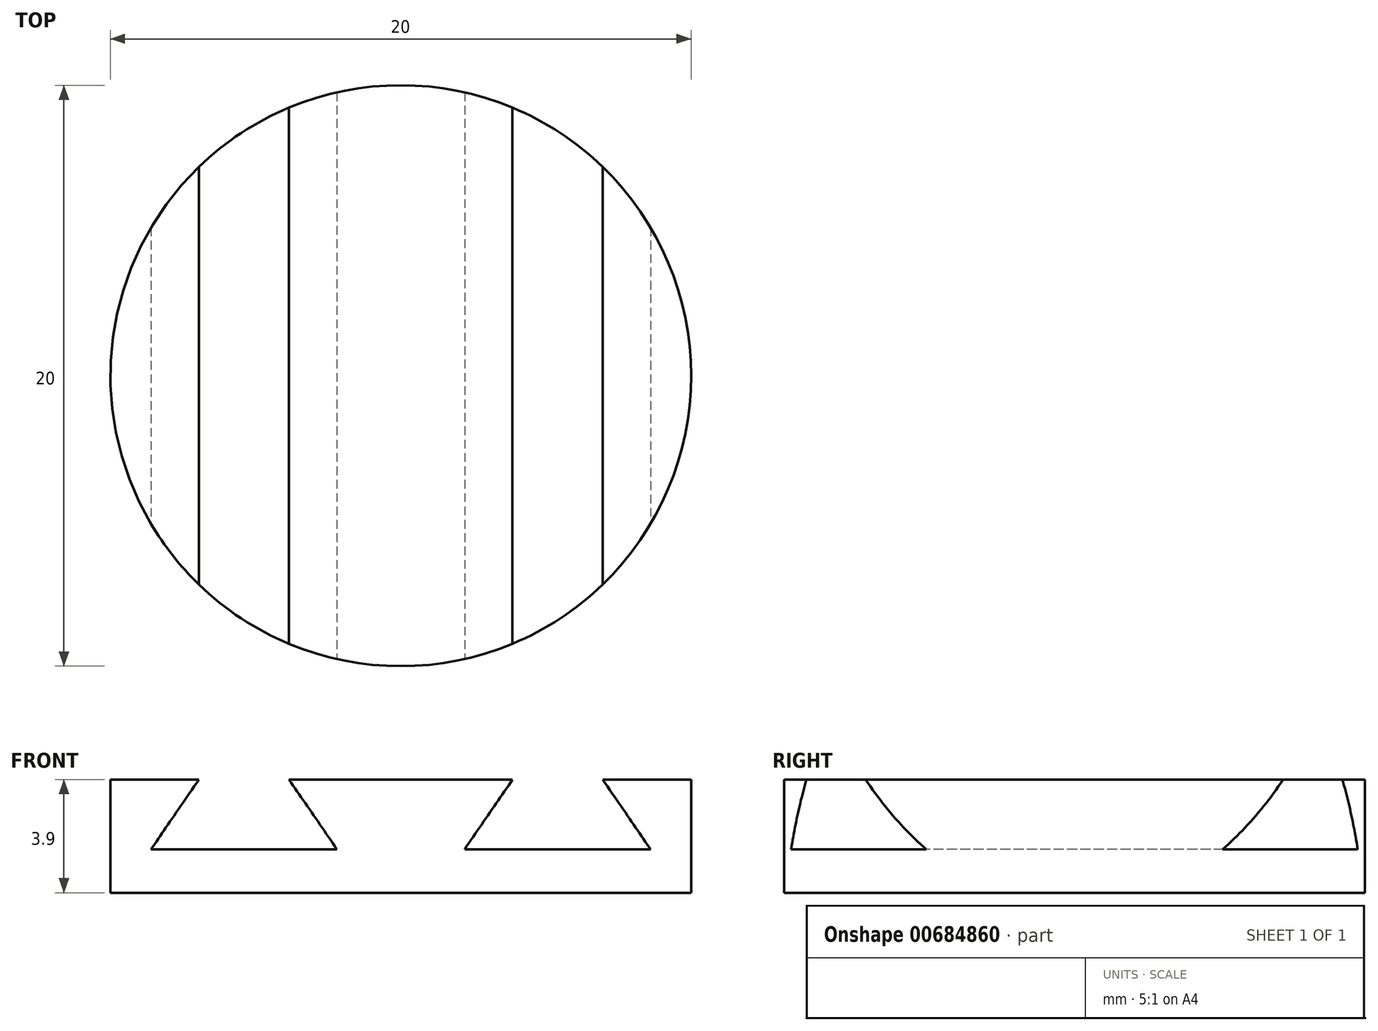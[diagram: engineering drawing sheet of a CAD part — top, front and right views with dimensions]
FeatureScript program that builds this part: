
annotation { "Feature Type Name" : "Feature", "Feature Type Description" : "" }
export const myFeature = defineFeature(function(context is Context, id is Id, definition is map)
    precondition{}
    {
        {
            var Q0;
            Q0=qCreatedBy(makeId("Top.planeOp"),FACE);
            var sketch = newSketch(context, id + "F0", { "sketchPlane" : qUnion([Q0])});
            skPoint(sketch, "E0", {"position": v(10, 0) * mm});
            skCircle(sketch, "E1", {"center": v(0, 0) * mm, "radius": 10 * mm});
            skSolve(sketch);
        }
        {
            var Q0;
            Q0=makeQuery(id+"F0.imprint","IMPRINT",FACE,{"disambiguationData":[TD([[makeQuery(id+"F0.imprint","IMPRINT",EDGE,{"derivedFrom":sQuery(id+"F0.wireOp",EDGE,"E1")}),1.0]])]});
            extrude(context, id + "F1", {"entities" : qUnion([Q0]), "depth" : 3.9 * mm, "offsetDistance" : 25 * mm});
        }
        {
            var Q0;
            Q0=qCreatedBy(makeId("Front.planeOp"),FACE);
            var sketch = newSketch(context, id + "F2", { "sketchPlane" : qUnion([Q0])});
            skLineSegment(sketch, "E2", {"start": v(15.37, 1.4) * mm, "end": v(-17.26, 1.4) * mm});
            skLineSegment(sketch, "E3", {"start": v(-6.95, 1.4) * mm, "end": v(-8.6, -1) * mm});
            skLineSegment(sketch, "E4", {"start": v(-3.85, 1.4) * mm, "end": v(-2.2, -1) * mm});
            skLineSegment(sketch, "E5", {"start": v(6.95, 1.4) * mm, "end": v(8.6, -1) * mm});
            skLineSegment(sketch, "E6", {"start": v(3.85, 1.4) * mm, "end": v(2.2, -1) * mm});
            skLineSegment(sketch, "E7", {"start": v(2.2, -1) * mm, "end": v(-2.2, -1) * mm});
            skLineSegment(sketch, "E8", {"start": v(-8.6, -1) * mm, "end": v(-11.8, -1) * mm});
            skLineSegment(sketch, "E9", {"start": v(-11.8, -1) * mm, "end": v(-11.8, 1.4) * mm});
            skLineSegment(sketch, "E10", {"start": v(8.6, -1) * mm, "end": v(10.84, -1) * mm});
            skLineSegment(sketch, "E11", {"start": v(10.84, -1) * mm, "end": v(10.84, 1.4) * mm});
            skLineSegment(sketch, "E12", {"start": v(-8.6, -1) * mm, "end": v(-2.2, -1) * mm});
            skLineSegment(sketch, "E13", {"start": v(2.2, -1) * mm, "end": v(8.6, -1) * mm});
            skSolve(sketch);
        }
        {
            var Q0;
            Q0=makeQuery(id+"F1.opExtrude","SWEPT_BODY",BODY,{"disambiguationData":[OSD([sQuery(id+"F0.wireOp",EDGE,"E1")])]});
            transform(context, id + "F3", {"entities" : qUnion([Q0]), "transformType" : TransformType.TRANSLATION_3D, "dx" : 0 * mm, "dy" : 0 * mm, "dz" : -2.5 * mm, "makeCopy" : false});
        }
        {
            var Q0;
            {var subQ0=sQuery(id+"F2.wireOp",EDGE,"E3");Q0=makeQuery(id+"F2.imprint","IMPRINT",FACE,{"disambiguationData":[TD([[makeQuery(id+"F2.imprint","IMPRINT",EDGE,{"derivedFrom":subQ0}),1.0]])]});}
            var Q1;
            {var subQ0=sQuery(id+"F2.wireOp",EDGE,"E5");Q1=makeQuery(id+"F2.imprint","IMPRINT",FACE,{"disambiguationData":[TD([[makeQuery(id+"F2.imprint","IMPRINT",EDGE,{"derivedFrom":subQ0}),-1.0]])]});}
            extrude(context, id + "F4", {"entities" : qUnion([Q0, Q1]), "operationType" : NewBodyOperationType.REMOVE, "oppositeDirection" : true, "depth" : 25 * mm, "offsetDistance" : 25 * mm});
        }
        {
            var Q0;
            Q0=makeQuery(id+"F4.boolean.opBoolean","COPY",FACE,{"derivedFrom":makeQuery(id+"F4.opExtrude","CAP_FACE",FACE,{"disambiguationData":[OSD([sQuery(id+"F2.wireOp",EDGE,"E2"),sQuery(id+"F2.wireOp",EDGE,"E5"),sQuery(id+"F2.wireOp",EDGE,"E6"),sQuery(id+"F2.wireOp",EDGE,"E13")])],"isStart":true})});
            var Q1;
            Q1=makeQuery(id+"F4.boolean.opBoolean","COPY",FACE,{"derivedFrom":makeQuery(id+"F4.opExtrude","CAP_FACE",FACE,{"disambiguationData":[OSD([sQuery(id+"F2.wireOp",EDGE,"E2"),sQuery(id+"F2.wireOp",EDGE,"E3"),sQuery(id+"F2.wireOp",EDGE,"E4"),sQuery(id+"F2.wireOp",EDGE,"E12")])],"isStart":true})});
            extrude(context, id + "F5", {"entities" : qUnion([Q0, Q1]), "operationType" : NewBodyOperationType.REMOVE, "oppositeDirection" : true, "depth" : 25 * mm, "offsetDistance" : 25 * mm});
        }
    });
